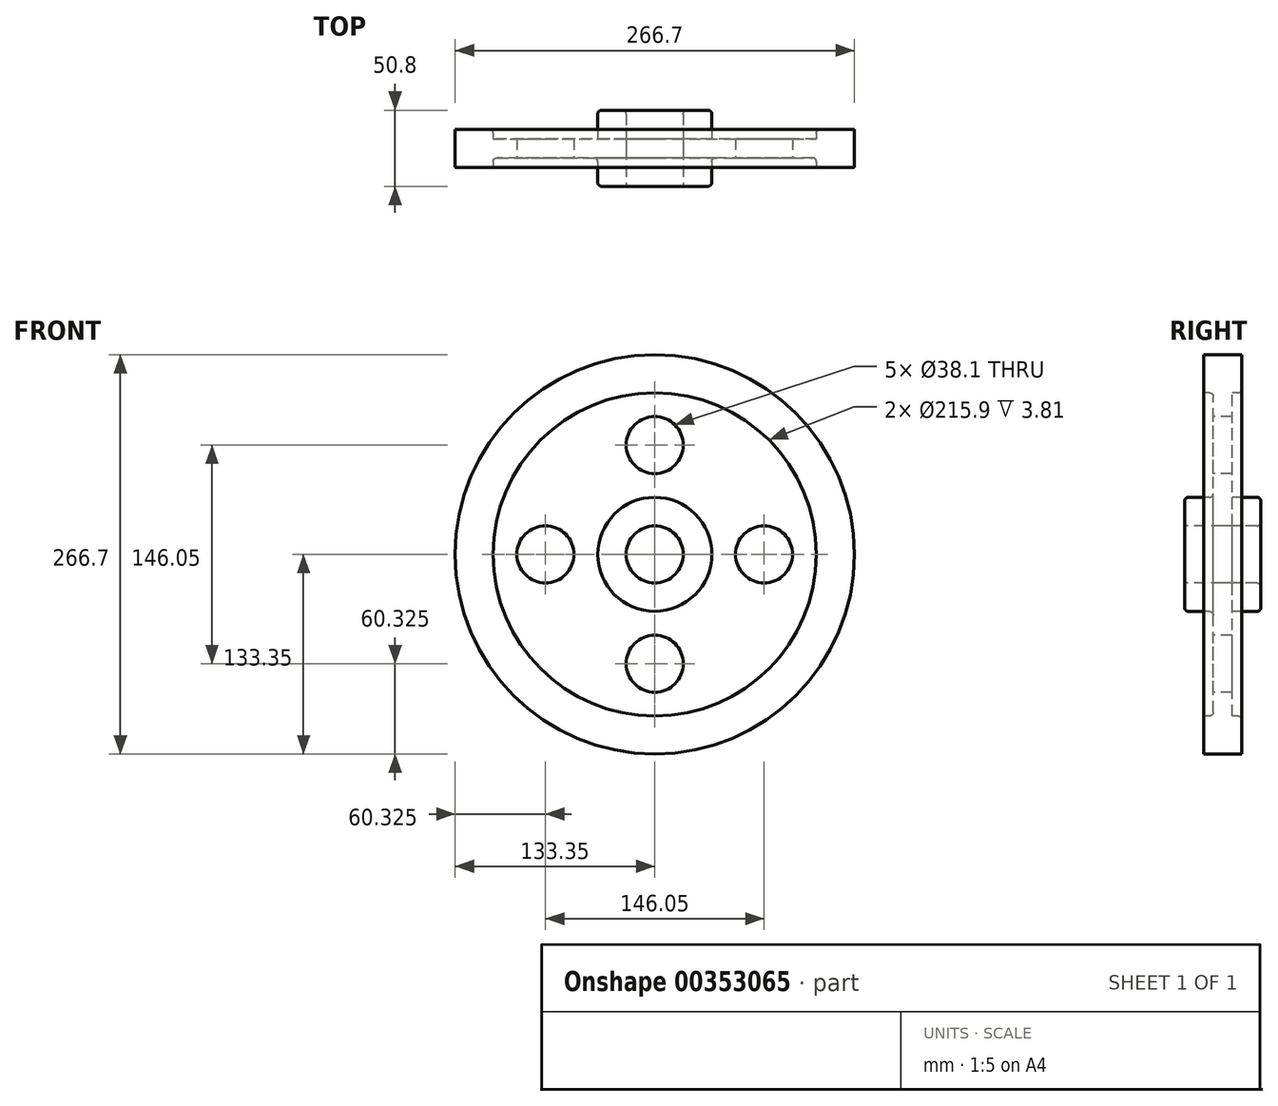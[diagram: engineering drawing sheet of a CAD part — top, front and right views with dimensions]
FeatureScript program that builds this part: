
annotation { "Feature Type Name" : "Feature", "Feature Type Description" : "" }
export const myFeature = defineFeature(function(context is Context, id is Id, definition is map)
    precondition{}
    {
        {
            var Q0;
            Q0=qCreatedBy(makeId("Right.planeOp"),FACE);
            var sketch = newSketch(context, id + "F0", { "sketchPlane" : qUnion([Q0])});
            skLineSegment(sketch, "E0", {"start": v(0, 0) * mm, "end": v(71.71, 0) * mm, "construction": true});
            skLineSegment(sketch, "E1.0", {"start": v(0, 19.05) * mm, "end": v(25.4, 19.05) * mm});
            skLineSegment(sketch, "E2.0", {"start": v(6.35, 38.1) * mm, "end": v(25.4, 38.1) * mm});
            skLineSegment(sketch, "E3.0", {"start": v(0, 133.35) * mm, "end": v(12.7, 133.35) * mm});
            skLineSegment(sketch, "E4", {"start": v(0, 0) * mm, "end": v(0, 73.03) * mm, "construction": true});
            skLineSegment(sketch, "E5", {"start": v(0, 0) * mm, "end": v(0, 133.35) * mm, "construction": true});
            skLineSegment(sketch, "E6", {"start": v(-171.7, 98.76) * mm, "end": v(-179.04, 102.63) * mm, "construction": true});
            skLineSegment(sketch, "E7.0", {"start": v(25.4, 19.05) * mm, "end": v(25.4, 38.1) * mm});
            skLineSegment(sketch, "E8.0", {"start": v(6.35, 38.1) * mm, "end": v(6.35, 107.95) * mm});
            skLineSegment(sketch, "E9.0", {"start": v(6.35, 107.95) * mm, "end": v(12.7, 107.95) * mm});
            skLineSegment(sketch, "E10.trimOffspring", {"start": v(12.7, 107.95) * mm, "end": v(12.7, 133.35) * mm});
            skLineSegment(sketch, "E11.MirrorCS", {"start": v(-25.4, 19.05) * mm, "end": v(-25.4, 38.1) * mm});
            skLineSegment(sketch, "E12.MirrorCS", {"start": v(-6.35, 38.1) * mm, "end": v(-25.4, 38.1) * mm});
            skLineSegment(sketch, "E13.MirrorCS", {"start": v(-6.35, 38.1) * mm, "end": v(-6.35, 107.95) * mm});
            skLineSegment(sketch, "E14.MirrorCS", {"start": v(-12.7, 107.95) * mm, "end": v(-12.7, 133.35) * mm});
            skLineSegment(sketch, "E15.MirrorCS", {"start": v(0, 133.35) * mm, "end": v(-12.7, 133.35) * mm});
            skLineSegment(sketch, "E16", {"start": v(-25.4, 19.05) * mm, "end": v(0, 19.05) * mm});
            skLineSegment(sketch, "E17", {"start": v(-12.7, 107.95) * mm, "end": v(-6.35, 107.95) * mm});
            skSolve(sketch);
        }
        {
            var Q0;
            Q0=makeQuery(id+"F0.imprint","IMPRINT",FACE,{"disambiguationData":[TD([[makeQuery(id+"F0.imprint","IMPRINT",EDGE,{"derivedFrom":sQuery(id+"F0.wireOp",EDGE,"E1.0")}),1.0]])]});
            var Q1;
            Q1=sQuery(id+"F0.wireOp",EDGE,"E0");
            revolve(context, id + "F1", {"entities" : qUnion([Q0]), "axis" : qUnion([Q1]), "revolveType" : RevolveType.FULL});
        }
        {
            var Q0;
            Q0=makeQuery(id+"F1.opRevolve","SWEPT_EDGE",EDGE,{"disambiguationData":[OSD([sQuery(id+"F0.wireOp",EDGE,"E9.0"),sQuery(id+"F0.wireOp",EDGE,"E10.trimOffspring")])]});
            var Q1;
            Q1=makeQuery(id+"F1.opRevolve","SWEPT_EDGE",EDGE,{"disambiguationData":[OSD([sQuery(id+"F0.wireOp",EDGE,"E13.MirrorCS"),sQuery(id+"F0.wireOp",EDGE,"E17")])]});
            var Q2;
            Q2=makeQuery(id+"F1.opRevolve","SWEPT_FACE",FACE,{"disambiguationData":[OSD([sQuery(id+"F0.wireOp",EDGE,"E13.MirrorCS")])]});
            var Q3;
            Q3=makeQuery(id+"F1.opRevolve","SWEPT_EDGE",EDGE,{"disambiguationData":[OSD([sQuery(id+"F0.wireOp",EDGE,"E2.0"),sQuery(id+"F0.wireOp",EDGE,"E7.0")])]});
            var Q4;
            Q4=makeQuery(id+"F1.opRevolve","SWEPT_EDGE",EDGE,{"disambiguationData":[OSD([sQuery(id+"F0.wireOp",EDGE,"E1.0"),sQuery(id+"F0.wireOp",EDGE,"E7.0")])]});
            var Q5;
            Q5=makeQuery(id+"F1.opRevolve","SWEPT_EDGE",EDGE,{"disambiguationData":[OSD([sQuery(id+"F0.wireOp",EDGE,"E11.MirrorCS"),sQuery(id+"F0.wireOp",EDGE,"E12.MirrorCS")])]});
            fillet(context, id + "F2", {"entities" : qUnion([Q0, Q1, Q2, Q3, Q4, Q5]), "radius" : 2.54 * mm, "tangentPropagation" : true, "allowEdgeOverflow" : false});
        }
        {
            var Q0;
            Q0=makeQuery(id+"F1.opRevolve","SWEPT_FACE",FACE,{"disambiguationData":[OSD([sQuery(id+"F0.wireOp",EDGE,"E13.MirrorCS")])]});
            var sketch = newSketch(context, id + "F3", { "sketchPlane" : qUnion([Q0])});
            skLineSegment(sketch, "E18", {"start": v(0, 0) * mm, "end": v(0, 73.03) * mm});
            skCircle(sketch, "E19", {"center": v(0, 73.03) * mm, "radius": 19.05 * mm});
            skCircle(sketch, "E20.1.0", {"center": v(-73.03, 0) * mm, "radius": 19.05 * mm});
            skCircle(sketch, "E20.2.0", {"center": v(0, -73.03) * mm, "radius": 19.05 * mm});
            skCircle(sketch, "E20.3.0", {"center": v(73.03, 0) * mm, "radius": 19.05 * mm});
            skPoint(sketch, "E20.center", {"position": v(0, 0) * mm});
            skSolve(sketch);
        }
        {
            var Q0;
            Q0=makeQuery(id+"F3.imprint","IMPRINT",FACE,{"disambiguationData":[TD([[makeQuery(id+"F3.imprint","IMPRINT",EDGE,{"derivedFrom":sQuery(id+"F3.wireOp",EDGE,"E20.1.0")}),1.0]])]});
            var Q1;
            Q1=makeQuery(id+"F3.imprint","IMPRINT",FACE,{"disambiguationData":[TD([[makeQuery(id+"F3.imprint","IMPRINT",EDGE,{"derivedFrom":sQuery(id+"F3.wireOp",EDGE,"E20.2.0")}),1.0]])]});
            var Q2;
            Q2=makeQuery(id+"F3.imprint","IMPRINT",FACE,{"disambiguationData":[TD([[makeQuery(id+"F3.imprint","IMPRINT",EDGE,{"derivedFrom":sQuery(id+"F3.wireOp",EDGE,"E20.3.0")}),1.0]])]});
            var Q3;
            Q3=makeQuery(id+"F3.imprint","IMPRINT",FACE,{"disambiguationData":[TD([[makeQuery(id+"F3.imprint","IMPRINT",EDGE,{"derivedFrom":sQuery(id+"F3.wireOp",EDGE,"E19")}),1.0]])]});
            extrude(context, id + "F4", {"entities" : qUnion([Q0, Q1, Q2, Q3]), "operationType" : NewBodyOperationType.REMOVE, "oppositeDirection" : true, "depth" : 25.4 * mm});
        }
    });
